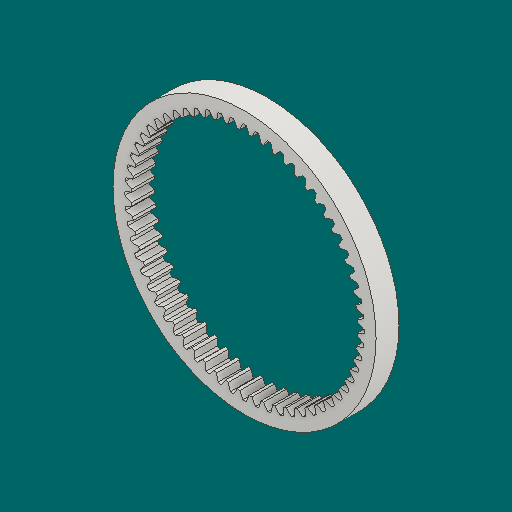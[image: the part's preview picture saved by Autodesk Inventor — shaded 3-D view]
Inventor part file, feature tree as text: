
AUTODESK INVENTOR PART (.ipt)
format: ipt  version: 2023.1 (Build 271208000, 208)  size: 473,600 bytes
history: native  units: in
note: dims shown in document units (in); Inventor stores cm internally (conversion verified against a paired STEP export)
features: other x12, plane x3, sketch x2
ambient origin geometry x8: Origin, YZ Plane, XZ Plane, XY Plane, X Axis, Y Axis, Z Axis, Center Point
bodies: Solid1 (feature_tree)
feature tree (17):
  other  "Spur Gear21_MIR.ipt"
  other  "Solid1::Spur Gear21_MIR.ipt"
  other  "TaggingFeature1"
  sketch  "Sketch1"  dims[d0=0.3937in]
  sketch  "Sketch2"  dims[d9=0.0in d14=0.0in d15=1.05in d16=0.0in d17=0.0in d18=0.0in d19=1.05in]
  plane  "XZ Plane_1"
  plane  "Work Plane2"
  plane  "Work Plane3"
  other  "Srf1"
  other  "Srf1::Derived"
  other  "Start plane iMate"
  other  "Distance iMate"
  other  "Mesh iMate"
  other  "Position iMate"
  other  "Axis iMate"
  other  "Mesh iMate2"
  other  "Align iMate"
